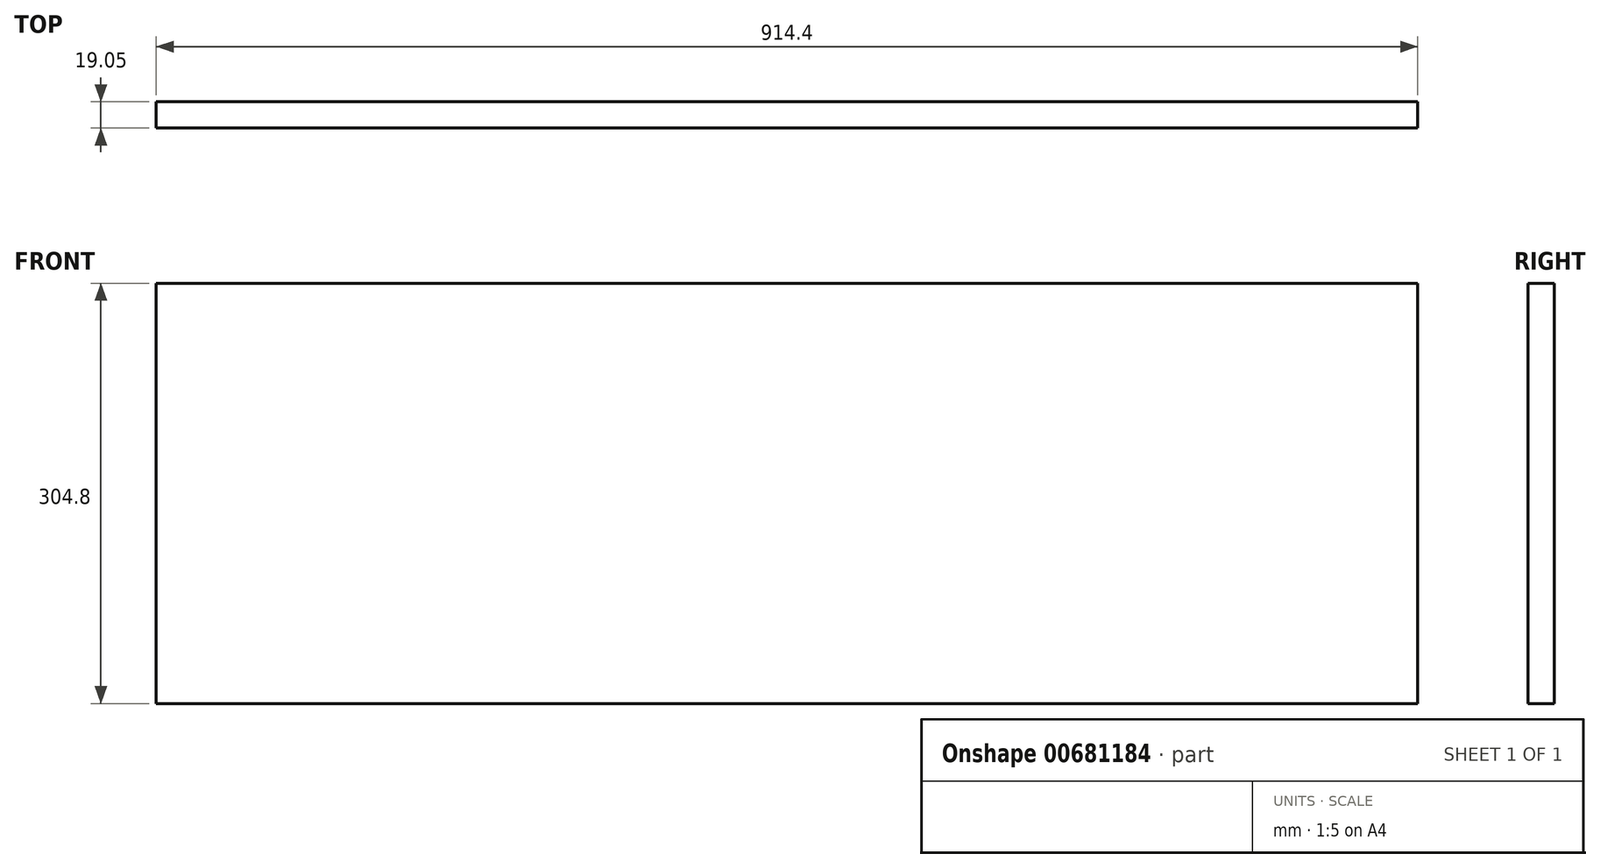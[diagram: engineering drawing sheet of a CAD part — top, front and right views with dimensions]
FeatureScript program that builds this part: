
annotation { "Feature Type Name" : "Feature", "Feature Type Description" : "" }
export const myFeature = defineFeature(function(context is Context, id is Id, definition is map)
    precondition{}
    {
        {
            var Q0;
            Q0=qCreatedBy(makeId("Front.planeOp"),FACE);
            var sketch = newSketch(context, id + "F0", { "sketchPlane" : qUnion([Q0])});
            skLineSegment(sketch, "E0.bottom", {"start": v(457.2, 152.4) * mm, "end": v(-457.2, 152.4) * mm});
            skLineSegment(sketch, "E0.top", {"start": v(457.2, -152.4) * mm, "end": v(-457.2, -152.4) * mm});
            skLineSegment(sketch, "E0.left", {"start": v(457.2, 152.4) * mm, "end": v(457.2, -152.4) * mm});
            skLineSegment(sketch, "E0.right", {"start": v(-457.2, 152.4) * mm, "end": v(-457.2, -152.4) * mm});
            skPoint(sketch, "E0.middle", {"position": v(0, 0) * mm});
            skSolve(sketch);
        }
        {
            var Q0;
            Q0=makeQuery(id+"F0.imprint","IMPRINT",FACE,{"disambiguationData":[TD([[makeQuery(id+"F0.imprint","IMPRINT",EDGE,{"derivedFrom":sQuery(id+"F0.wireOp",EDGE,"E0.bottom")}),1.0]])]});
            extrude(context, id + "F1", {"entities" : qUnion([Q0]), "depth" : 19.05 * mm, "offsetDistance" : 25.4 * mm});
        }
    });
